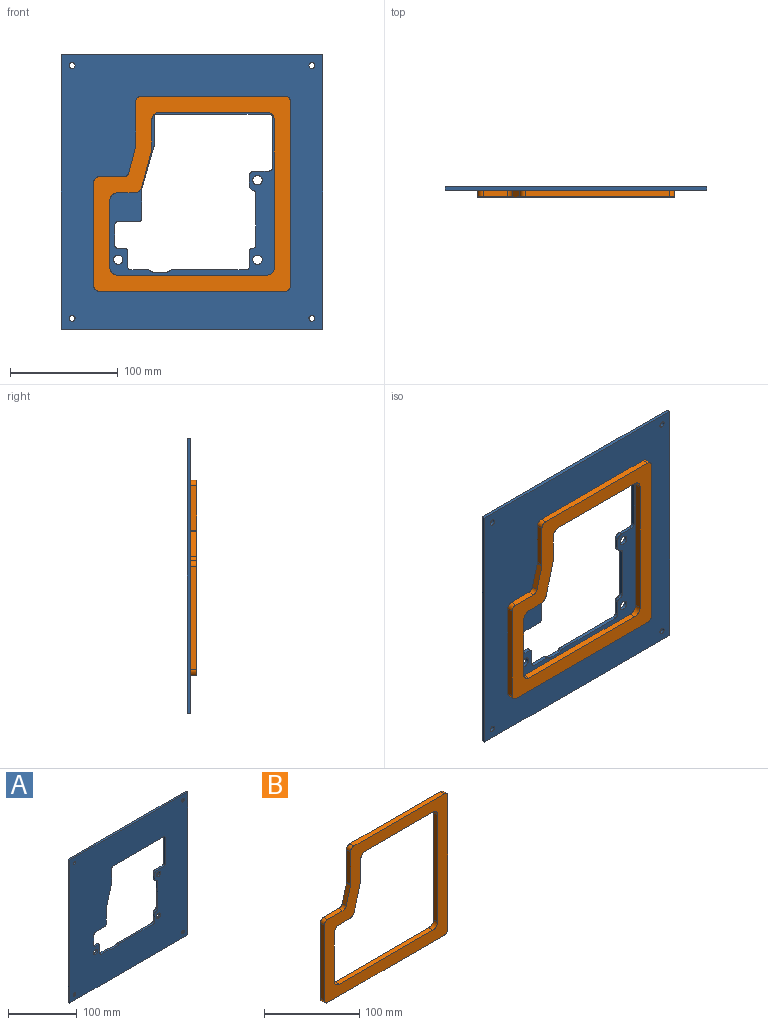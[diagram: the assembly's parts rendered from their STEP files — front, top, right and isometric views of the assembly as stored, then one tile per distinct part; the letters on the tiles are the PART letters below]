
ASSEMBLY  parts=2 mates=1
PART A: 51 faces, bbox 243x3.2x255 mm
  f0: plane 255x243mm, normal (0,-1,0), area 45383.6mm2, adj f2,f3,f4,f5,f6,f7,f8,f9
  f1: plane 255x243mm, normal (0,1,0), area 45383.6mm2, adj f2,f3,f4,f5,f6,f7,f8,f9
  f2: plane 243x3.18mm, normal (0,0,-1), area 771.5mm2, adj f0,f1,f45,f46
  f3: plane 243x3.18mm, normal (0,0,1), area 771.5mm2, adj f0,f1,f45,f46
  f4: plane 13.5x3.18mm, normal (0,0,1), area 42.9mm2, adj f0,f1,f22,f37
  f5: plane 47x3.18mm, normal (-1,0,0), area 149.2mm2, adj f0,f1,f22,f23
  f6: plane 104x3.18mm, normal (0,0,-1), area 330.2mm2, adj f0,f1,f23,f24
  f7: plane 26.58x3.18mm, normal (1,0,0), area 84.4mm2, adj f0,f1,f24,f25
  f8: plane 39.19x11.27mm, normal (0.96,0,-0.28), area 129.5mm2, adj f0,f1,f25,f26
  f9: plane 26.58x3.18mm, normal (1,0,0), area 84.4mm2, adj f0,f1,f26,f27
  f10: plane 19x3.18mm, normal (0,0,-1), area 60.3mm2, adj f0,f1,f27,f28
  f11: plane 19x3.18mm, normal (1,0,0), area 60.3mm2, adj f0,f1,f28,f29
  f12: plane 6x3.18mm, normal (0,0,1), area 19.1mm2, adj f0,f1,f29,f30
  f13: plane 14x3.18mm, normal (1,0,0), area 44.5mm2, adj f0,f1,f30,f31
  f14: plane 16.17x3.18mm, normal (0,0,1), area 51.3mm2, adj f0,f1,f31,f38
  f15: plane 3.18x0.03mm, normal (0.74,0,0.67), area 0.1mm2, adj f0,f1,f38,f40
  f16: plane 12.71x3.18mm, normal (0,0,1), area 40.4mm2, adj f0,f1,f40,f41
  f17: plane 3.18x0.03mm, normal (-0.74,0,0.67), area 0.1mm2, adj f0,f1,f39,f41
  f18: plane 69.17x3.18mm, normal (0,0,1), area 219.6mm2, adj f0,f1,f32,f39
  f19: plane 14x3.18mm, normal (-1,0,0), area 44.5mm2, adj f0,f1,f32,f34
  f20: plane 48x3.18mm, normal (-1,0,0), area 152.4mm2, adj f0,f1,f33,f35
  f21: plane 8.25x3.18mm, normal (-1,0,0), area 26.2mm2, adj f0,f1,f36,f37
  f22: cylinder r=3mm len=3.18mm, axis (0,-1,0), area 15mm2, adj f0,f1,f4,f5
  f23: cylinder r=3mm len=3.18mm, axis (0,1,0), area 15mm2, adj f0,f1,f5,f6
  f24: cylinder r=3mm len=3.18mm, axis (0,1,0), area 15mm2, adj f0,f1,f6,f7
  f25: cylinder r=3mm len=3.18mm, axis (0,1,0), area 2.7mm2, adj f0,f1,f7,f8
  f26: cylinder r=3mm len=3.18mm, axis (0,1,0), area 2.7mm2, adj f0,f1,f8,f9
  f27: cylinder r=3mm len=3.18mm, axis (0,-1,0), area 15mm2, adj f0,f1,f9,f10
  f28: cylinder r=3mm len=3.18mm, axis (0,1,0), area 15mm2, adj f0,f1,f10,f11
  f29: cylinder r=3mm len=3.18mm, axis (0,-1,0), area 15mm2, adj f0,f1,f11,f12
  f30: cylinder r=3mm len=3.18mm, axis (0,1,0), area 15mm2, adj f0,f1,f12,f13
  f31: cylinder r=3mm len=3.18mm, axis (0,1,0), area 15mm2, adj f0,f1,f13,f14
  f32: cylinder r=3mm len=3.18mm, axis (0,1,0), area 15mm2, adj f0,f1,f18,f19
  f33: cylinder r=3mm len=3.18mm, axis (0,1,0), area 15mm2, adj f0,f1,f20,f34
  f34: cylinder r=3mm len=3.18mm, axis (0,1,0), area 15mm2, adj f0,f1,f19,f33
  f35: cylinder r=3mm len=3.18mm, axis (0,-1,0), area 12.6mm2, adj f0,f1,f20,f36
  f36: cylinder r=5mm len=4.84mm, axis (0,-1,0), area 20.9mm2, adj f0,f1,f21,f35
  f37: cylinder r=5mm len=5mm, axis (0,1,0), area 24.9mm2, adj f0,f1,f4,f21
  f38: cylinder r=3mm len=3.18mm, axis (0,1,0), area 7.9mm2, adj f0,f1,f14,f15
  f39: cylinder r=3mm len=3.18mm, axis (0,-1,0), area 7.9mm2, adj f0,f1,f17,f18
  f40: cylinder r=3mm len=3.18mm, axis (0,1,0), area 7.9mm2, adj f0,f1,f15,f16
  f41: cylinder r=3mm len=3.18mm, axis (0,-1,0), area 7.9mm2, adj f0,f1,f16,f17
  f42: cylinder r=4.38mm len=8.75mm, axis (0,-1,0), area 87.3mm2, adj f0,f1
  f43: cylinder r=4.38mm len=8.75mm, axis (0,-1,0), area 87.3mm2, adj f0,f1
  f44: cylinder r=4.38mm len=8.75mm, axis (0,-1,0), area 87.3mm2, adj f0,f1
  f45: plane 255x3.18mm, normal (1,0,0), area 809.6mm2, adj f0,f1,f2,f3
  f46: plane 255x3.18mm, normal (-1,0,0), area 809.6mm2, adj f0,f1,f2,f3
  f47: cylinder r=2.75mm len=5.5mm, axis (0,-1,0), area 54.9mm2, adj f0,f1
  f48: cylinder r=2.75mm len=5.5mm, axis (0,-1,0), area 54.9mm2, adj f0,f1
  f49: cylinder r=2.75mm len=5.5mm, axis (0,-1,0), area 54.9mm2, adj f0,f1
  f50: cylinder r=2.75mm len=5.5mm, axis (0,-1,0), area 54.9mm2, adj f0,f1
PART B: 29 faces, bbox 183x6x181.5 mm
  f0: plane 183x181.5mm, normal (0,-1,0), area 9938.4mm2, adj f2,f3,f4,f5,f6,f7,f8,f9
  f1: plane 183x181.5mm, normal (0,1,0), area 9938.4mm2, adj f2,f3,f4,f5,f6,f7,f8,f9
  f2: plane 15.7x6mm, normal (0,0,-1), area 94.2mm2, adj f0,f1,f9,f14
  f3: plane 62.5x6mm, normal (1,0,0), area 375mm2, adj f0,f1,f9,f10
  f4: plane 139x6mm, normal (0,0,1), area 834mm2, adj f0,f1,f10,f11
  f5: plane 137.5x6mm, normal (-1,0,0), area 825mm2, adj f0,f1,f11,f12
  f6: plane 100x6mm, normal (0,0,-1), area 600mm2, adj f0,f1,f12,f13
  f7: plane 27.2x6mm, normal (1,0,0), area 163.2mm2, adj f0,f1,f8,f13
  f8: plane 35.61x9.54mm, normal (0.97,0,-0.26), area 221.2mm2, adj f0,f1,f7,f14
  f9: cylinder r=7mm len=7mm, axis (0,1,0), area 66mm2, adj f0,f1,f2,f3
  f10: cylinder r=7mm len=7mm, axis (0,1,0), area 66mm2, adj f0,f1,f3,f4
  f11: cylinder r=7mm len=7mm, axis (0,1,0), area 66mm2, adj f0,f1,f4,f5
  f12: cylinder r=7mm len=7mm, axis (0,1,0), area 66mm2, adj f0,f1,f5,f6
  f13: cylinder r=7mm len=7mm, axis (0,1,0), area 66mm2, adj f0,f1,f6,f7
  f14: cylinder r=7mm len=6.76mm, axis (0,-1,0), area 55mm2, adj f0,f1,f2,f8
  f15: plane 134x6mm, normal (0,0,1), area 804mm2, adj f0,f1,f22,f28
  f16: plane 171.5x6mm, normal (1,0,0), area 1029mm2, adj f0,f1,f22,f23
  f17: plane 173x6mm, normal (0,0,-1), area 1038mm2, adj f0,f1,f23,f24
  f18: plane 96.5x6mm, normal (-1,0,0), area 579mm2, adj f0,f1,f24,f25
  f19: plane 22.72x6mm, normal (0,0,1), area 136.3mm2, adj f0,f1,f25,f26
  f20: plane 23.43x6.28mm, normal (-0.97,0,0.26), area 145.5mm2, adj f0,f1,f26,f27
  f21: plane 41.57x6mm, normal (-1,0,0), area 249.4mm2, adj f0,f1,f27,f28
  f22: cylinder r=5mm len=6mm, axis (0,-1,0), area 47.1mm2, adj f0,f1,f15,f16
  f23: cylinder r=5mm len=6mm, axis (0,-1,0), area 47.1mm2, adj f0,f1,f16,f17
  f24: cylinder r=5mm len=6mm, axis (0,-1,0), area 47.1mm2, adj f0,f1,f17,f18
  f25: cylinder r=5mm len=6mm, axis (0,-1,0), area 47.1mm2, adj f0,f1,f18,f19
  f26: cylinder r=5mm len=6mm, axis (0,1,0), area 39.3mm2, adj f0,f1,f19,f20
  f27: cylinder r=5mm len=6mm, axis (0,1,0), area 7.9mm2, adj f0,f1,f20,f21
  f28: cylinder r=5mm len=6mm, axis (0,-1,0), area 47.1mm2, adj f0,f1,f15,f21
PLACE A t=(-66.48,-121.04,43.88)mm
PLACE B t=(-67.83,-124.22,42.25)mm
MATE planar A.f38 <-> B.f1  axis (0,-1,0) through (-108.56,-124.22,-31.62)mm
